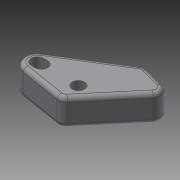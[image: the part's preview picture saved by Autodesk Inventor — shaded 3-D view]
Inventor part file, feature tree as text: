
AUTODESK INVENTOR PART (.ipt)
format: ipt  version: 2018 (Build 220112000, 112)  size: 155,648 bytes
history: native  units: mm
features: extrude x3, sketch x3, other x1, fillet x1
ambient origin geometry x8: Origin, YZ Plane, XZ Plane, XY Plane, X Axis, Y Axis, Z Axis, Center Point
bodies: Body1 (feature_tree)
feature tree (8):
  other  "ソリッド1"
  extrude  "押し出し1"  Depth=2.0mm
  extrude  "押し出し3"  Depth=6.5mm TaperAngle=0.0deg
  extrude  "押し出し5"  Depth=3.0mm
  fillet  "フィレット2"  Radius=1.0mm
  sketch  "スケッチ1"
  sketch  "スケッチ3"
  sketch  "スケッチ5"
